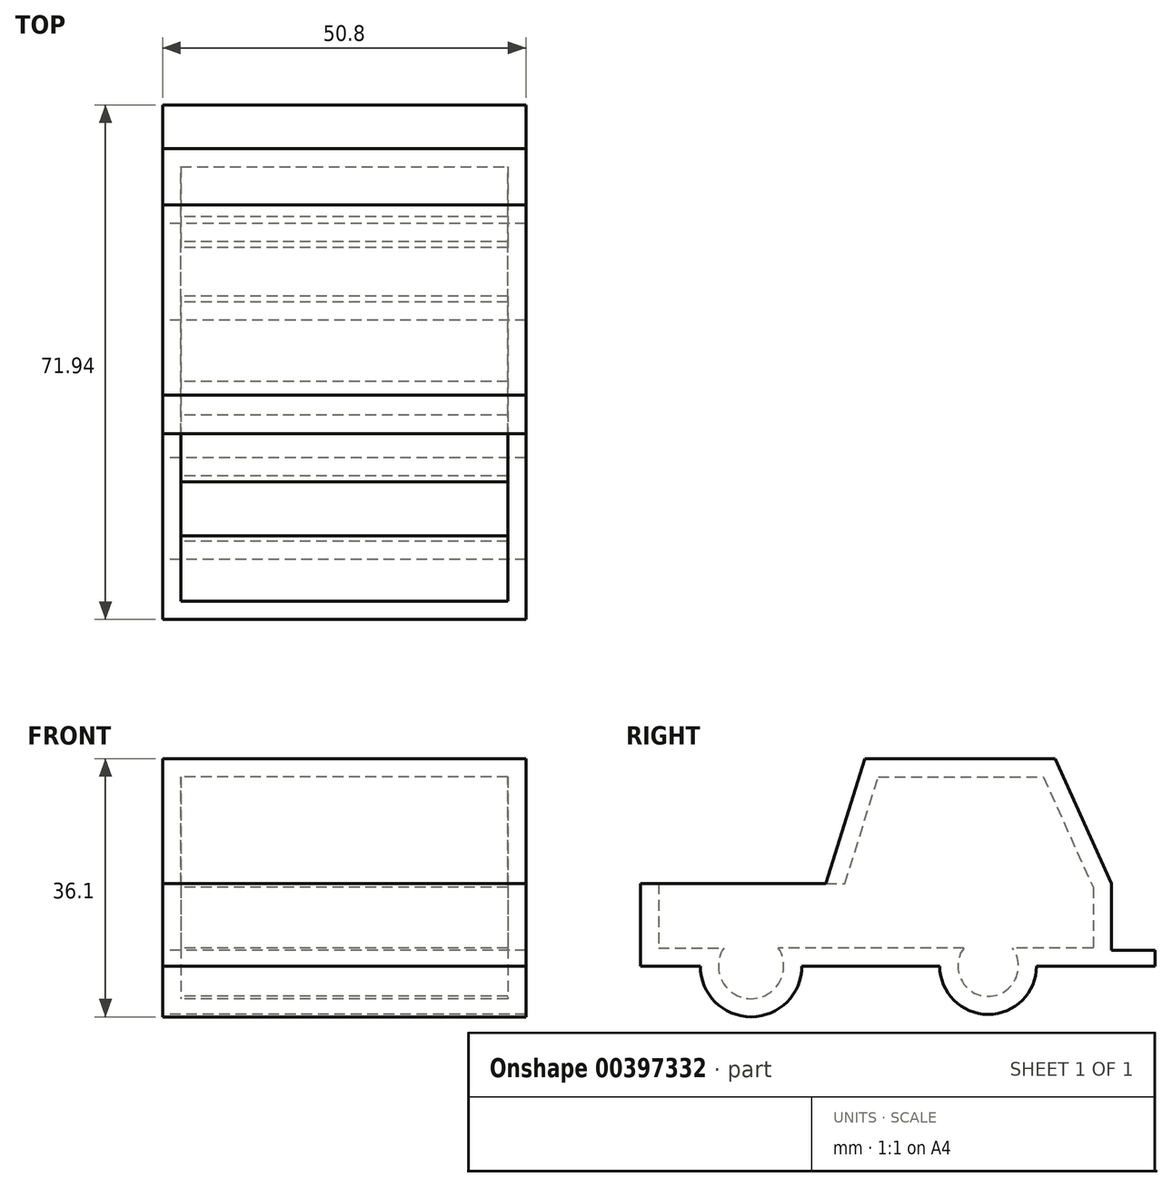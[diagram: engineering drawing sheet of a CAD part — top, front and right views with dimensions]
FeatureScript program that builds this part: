
annotation { "Feature Type Name" : "Feature", "Feature Type Description" : "" }
export const myFeature = defineFeature(function(context is Context, id is Id, definition is map)
    precondition{}
    {
        {
            var Q0;
            Q0=qCreatedBy(makeId("Right.planeOp"),FACE);
            var sketch = newSketch(context, id + "F0", { "sketchPlane" : qUnion([Q0])});
            skLineSegment(sketch, "E0", {"start": v(-58, 0) * mm, "end": v(-32.05, 0) * mm});
            skLineSegment(sketch, "E1", {"start": v(-58, 0) * mm, "end": v(-58, -11.55) * mm});
            skLineSegment(sketch, "E2", {"start": v(-58, -11.55) * mm, "end": v(-42.51, -11.55) * mm});
            skLineSegment(sketch, "E3", {"start": v(-32.05, 0) * mm, "end": v(-26.6, 17.44) * mm});
            skLineSegment(sketch, "E4", {"start": v(-26.6, 17.44) * mm, "end": v(0, 17.44) * mm});
            skLineSegment(sketch, "E5", {"start": v(0, 17.44) * mm, "end": v(7.85, 0) * mm});
            skLineSegment(sketch, "E6", {"start": v(7.85, 0) * mm, "end": v(7.85, -11.55) * mm});
            skLineSegment(sketch, "E7", {"start": v(7.85, -11.55) * mm, "end": v(-42.51, -11.55) * mm});
            skLineSegment(sketch, "E8", {"start": v(7.85, -9.37) * mm, "end": v(13.95, -9.37) * mm});
            skLineSegment(sketch, "E9", {"start": v(13.95, -9.37) * mm, "end": v(13.95, -11.55) * mm});
            skLineSegment(sketch, "E10", {"start": v(13.95, -11.55) * mm, "end": v(7.85, -11.55) * mm});
            skCircle(sketch, "E11", {"center": v(-42.51, -11.55) * mm, "radius": 7.1 * mm});
            skCircle(sketch, "E12", {"center": v(-9.37, -11.55) * mm, "radius": 6.77 * mm});
            skLineSegment(sketch, "E13", {"start": v(-32.05, 0) * mm, "end": v(7.85, 0) * mm});
            skLineSegment(sketch, "E14", {"start": v(-12.1, 0) * mm, "end": v(-12.1, 17.44) * mm});
            skSolve(sketch);
        }
        {
            var Q0;
            Q0 = qSketchRegion(id + "F0", true);
            extrude(context, id + "F1", {"entities" : qUnion([Q0]), "depth" : 50.8 * mm});
        }
        {
            var Q0;
            Q0=makeQuery(id+"F1.opExtrude","SWEPT_FACE",FACE,{"disambiguationData":[OSD([sQuery(id+"F0.wireOp",EDGE,"E0")])]});
            shell(context, id + "F2", {"entities" : qUnion([Q0]), "thickness" : 2.54 * mm});
        }
    });
